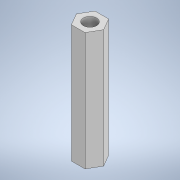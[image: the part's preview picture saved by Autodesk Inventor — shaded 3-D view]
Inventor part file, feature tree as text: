
AUTODESK INVENTOR PART (.ipt)
format: ipt  version: 2020 (Build 240168000, 168)  size: 106,496 bytes
history: native  units: mm
features: sketch x3, hole x2, extrude x1
ambient origin geometry x8: Origin, YZ Plane, XZ Plane, XY Plane, X Axis, Y Axis, Z Axis, Center Point
bodies: Solid1 (feature_tree)
feature tree (6):
  extrude  "Extrusion1"  Depth=30.0mm TaperAngle=0.0deg
  hole  "Hole1"  [1 undecoded]
  hole  "Hole2"  [1 undecoded]
  sketch  "Sketch1"  dims[d0=6.0mm d1=30.0mm d2=0.0mm]
  sketch  "Sketch2"  dims[d3=3.4mm d4=6.0mm d5=11.0mm d6=2.6mm d7=90.0deg d8=4.0mm d9=20.594885mm]
  sketch  "Sketch3"  dims[d10=3.4mm d11=6.0mm d12=11.0mm d13=2.6mm d14=90.0deg d15=4.0mm d16=20.594885mm]
note: 2 required parameter values undecoded (feature->parameter linkage not recoverable at this tier; creation-order binding heuristic only, values carry confidence <= 0.55)
